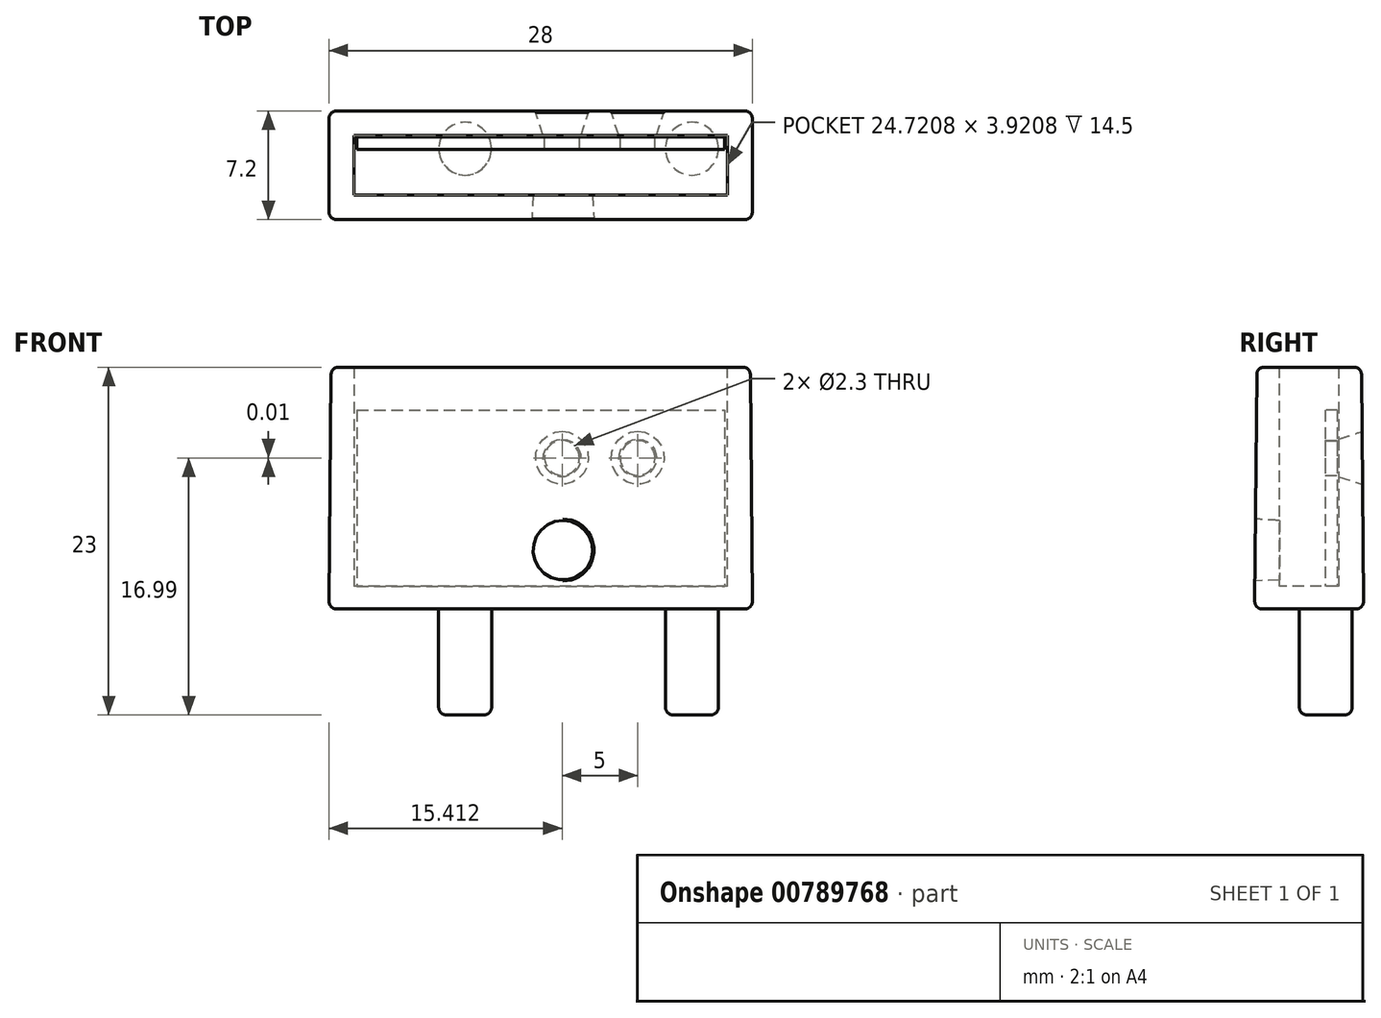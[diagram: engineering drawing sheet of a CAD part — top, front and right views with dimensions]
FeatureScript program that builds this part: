
annotation { "Feature Type Name" : "Feature", "Feature Type Description" : "" }
export const myFeature = defineFeature(function(context is Context, id is Id, definition is map)
    precondition{}
    {
        {
            var Q0;
            Q0=qCreatedBy(makeId("Top.planeOp"),FACE);
            var sketch = newSketch(context, id + "F0", { "sketchPlane" : qUnion([Q0])});
            skLineSegment(sketch, "E0.bottom", {"start": v(-11, 6) * mm, "end": v(17, 6) * mm});
            skLineSegment(sketch, "E0.top", {"start": v(-11, -1.2) * mm, "end": v(17, -1.2) * mm});
            skLineSegment(sketch, "E0.left", {"start": v(-11, 6) * mm, "end": v(-11, -1.2) * mm});
            skLineSegment(sketch, "E0.right", {"start": v(17, 6) * mm, "end": v(17, -1.2) * mm});
            skSolve(sketch);
        }
        {
            var Q0;
            Q0 = qSketchRegion(id + "F0", true);
            extrude(context, id + "F1", {"entities" : qUnion([Q0]), "depth" : 16 * mm, "offsetDistance" : 25 * mm, "hasDraft" : true, "draftAngle" : 0.5 * degree, "draftPullDirection" : true});
        }
        {
            var Q0;
            Q0=makeQuery(id+"F1.opExtrude","CAP_FACE",FACE,{"disambiguationData":[OSD([sQuery(id+"F0.wireOp",EDGE,"E0.bottom"),sQuery(id+"F0.wireOp",EDGE,"E0.top"),sQuery(id+"F0.wireOp",EDGE,"E0.left"),sQuery(id+"F0.wireOp",EDGE,"E0.right")])],"isStart":false});
            var sketch = newSketch(context, id + "F2", { "sketchPlane" : qUnion([Q0])});
            skLineSegment(sketch, "E1.bottom", {"start": v(-9.36, 4.36) * mm, "end": v(15.36, 4.36) * mm});
            skLineSegment(sketch, "E1.top", {"start": v(-9.36, 0.44) * mm, "end": v(15.36, 0.44) * mm});
            skLineSegment(sketch, "E1.left", {"start": v(-9.36, 4.36) * mm, "end": v(-9.36, 0.44) * mm});
            skLineSegment(sketch, "E1.right", {"start": v(15.36, 4.36) * mm, "end": v(15.36, 0.44) * mm});
            skSolve(sketch);
        }
        {
            var Q0;
            Q0=makeQuery(id+"F1.opExtrude","CAP_FACE",FACE,{"disambiguationData":[OSD([sQuery(id+"F0.wireOp",EDGE,"E0.bottom"),sQuery(id+"F0.wireOp",EDGE,"E0.top"),sQuery(id+"F0.wireOp",EDGE,"E0.left"),sQuery(id+"F0.wireOp",EDGE,"E0.right")])],"isStart":true});
            var sketch = newSketch(context, id + "F3", { "sketchPlane" : qUnion([Q0])});
            skCircle(sketch, "E2", {"center": v(13, -3.5) * mm, "radius": 1.75 * mm});
            skCircle(sketch, "E3", {"center": v(-2, -3.5) * mm, "radius": 1.75 * mm});
            skSolve(sketch);
        }
        {
            var Q0;
            Q0 = qSketchRegion(id + "F3", true);
            extrude(context, id + "F4", {"entities" : qUnion([Q0]), "operationType" : NewBodyOperationType.ADD, "depth" : 7 * mm, "offsetDistance" : 25 * mm});
        }
        {
            var Q0;
            Q0=makeQuery(id+"F1.opExtrude","SWEPT_FACE",FACE,{"disambiguationData":[OSD([sQuery(id+"F0.wireOp",EDGE,"E0.bottom")])]});
            var sketch = newSketch(context, id + "F5", { "sketchPlane" : qUnion([Q0])});
            skCircle(sketch, "E4", {"center": v(-6.73, 22.88) * mm, "radius": 1.75 * mm});
            skSolve(sketch);
        }
        {
            var Q0;
            Q0 = qSketchRegion(id + "F5", true);
            extrude(context, id + "F6", {"entities" : qUnion([Q0]), "operationType" : NewBodyOperationType.REMOVE, "oppositeDirection" : true, "depth" : 1.6 * mm, "offsetDistance" : 25 * mm, "hasDraft" : true, "draftAngle" : 18 * degree, "draftPullDirection" : true});
        }
        {
            var Q0;
            Q0=makeQuery(id+"F1.opExtrude","SWEPT_FACE",FACE,{"disambiguationData":[OSD([sQuery(id+"F0.wireOp",EDGE,"E0.bottom")])]});
            var sketch = newSketch(context, id + "F7", { "sketchPlane" : qUnion([Q0])});
            skCircle(sketch, "E5", {"center": v(-9.41, 9.95) * mm, "radius": 1.75 * mm});
            skCircle(sketch, "E6", {"center": v(-4.41, 9.95) * mm, "radius": 1.75 * mm});
            skSolve(sketch);
        }
        {
            var Q0;
            Q0 = qSketchRegion(id + "F7", true);
            extrude(context, id + "F8", {"entities" : qUnion([Q0]), "operationType" : NewBodyOperationType.REMOVE, "oppositeDirection" : true, "depth" : 1.7 * mm, "offsetDistance" : 25 * mm, "hasDraft" : true, "draftAngle" : 18 * degree, "draftPullDirection" : true});
        }
        {
            var Q0;
            Q0 = qSketchRegion(id + "F2", true);
            extrude(context, id + "F9", {"entities" : qUnion([Q0]), "operationType" : NewBodyOperationType.REMOVE, "oppositeDirection" : true, "depth" : 14.5 * mm, "offsetDistance" : 25 * mm, "hasDraft" : true, "draftAngle" : 0 * degree, "draftPullDirection" : true});
        }
        {
            var Q0;
            Q0=makeQuery(id+"F9.boolean.opBoolean","COPY",FACE,{"derivedFrom":makeQuery(id+"F9.opExtrude","CAP_FACE",FACE,{"disambiguationData":[OSD([sQuery(id+"F2.wireOp",EDGE,"E1.bottom"),sQuery(id+"F2.wireOp",EDGE,"E1.top"),sQuery(id+"F2.wireOp",EDGE,"E1.left"),sQuery(id+"F2.wireOp",EDGE,"E1.right")])],"isStart":false})});
            var sketch = newSketch(context, id + "F10", { "sketchPlane" : qUnion([Q0])});
            skLineSegment(sketch, "E7.bottom", {"start": v(-9.16, 4.26) * mm, "end": v(15.16, 4.26) * mm});
            skLineSegment(sketch, "E7.top", {"start": v(-9.16, 3.46) * mm, "end": v(15.16, 3.46) * mm});
            skLineSegment(sketch, "E7.left", {"start": v(-9.16, 4.26) * mm, "end": v(-9.16, 3.46) * mm});
            skLineSegment(sketch, "E7.right", {"start": v(15.16, 4.26) * mm, "end": v(15.16, 3.46) * mm});
            skSolve(sketch);
        }
        {
            var Q0;
            Q0 = qSketchRegion(id + "F10", true);
            extrude(context, id + "F11", {"entities" : qUnion([Q0]), "depth" : 11.66 * mm, "offsetDistance" : 25 * mm});
        }
        {
            var Q0;
            Q0=makeQuery(id+"F11.opExtrude","SWEPT_FACE",FACE,{"disambiguationData":[OSD([sQuery(id+"F10.wireOp",EDGE,"E7.bottom")])]});
            var sketch = newSketch(context, id + "F12", { "sketchPlane" : qUnion([Q0])});
            skCircle(sketch, "E8", {"center": v(-9.41, 9.99) * mm, "radius": 1.15 * mm});
            skCircle(sketch, "E9", {"center": v(-4.41, 10) * mm, "radius": 1.15 * mm});
            skSolve(sketch);
        }
        {
            var Q0;
            Q0 = qSketchRegion(id + "F12", true);
            extrude(context, id + "F13", {"entities" : qUnion([Q0]), "operationType" : NewBodyOperationType.REMOVE, "oppositeDirection" : true, "depth" : 1 * mm, "offsetDistance" : 25 * mm});
        }
        {
            var Q0;
            Q0=makeQuery(id+"F1.opExtrude","CAP_EDGE",EDGE,{"disambiguationData":[OSD([sQuery(id+"F0.wireOp",EDGE,"E0.bottom")])],"isStart":false});
            var Q1;
            Q1=makeQuery(id+"F1.opExtrude","CAP_EDGE",EDGE,{"disambiguationData":[OSD([sQuery(id+"F0.wireOp",EDGE,"E0.left")])],"isStart":false});
            var Q2;
            Q2=makeQuery(id+"F1.opExtrude","SWEPT_EDGE",EDGE,{"disambiguationData":[OSD([sQuery(id+"F0.wireOp",EDGE,"E0.bottom"),sQuery(id+"F0.wireOp",EDGE,"E0.left")])]});
            var Q3;
            Q3=makeQuery(id+"F1.opExtrude","CAP_EDGE",EDGE,{"disambiguationData":[OSD([sQuery(id+"F0.wireOp",EDGE,"E0.bottom")])],"isStart":true});
            var Q4;
            Q4=makeQuery(id+"F1.opExtrude","SWEPT_EDGE",EDGE,{"disambiguationData":[OSD([sQuery(id+"F0.wireOp",EDGE,"E0.bottom"),sQuery(id+"F0.wireOp",EDGE,"E0.right")])]});
            var Q5;
            Q5=makeQuery(id+"F1.opExtrude","SWEPT_EDGE",EDGE,{"disambiguationData":[OSD([sQuery(id+"F0.wireOp",EDGE,"E0.top"),sQuery(id+"F0.wireOp",EDGE,"E0.left")])]});
            var Q6;
            Q6=makeQuery(id+"F1.opExtrude","CAP_EDGE",EDGE,{"disambiguationData":[OSD([sQuery(id+"F0.wireOp",EDGE,"E0.left")])],"isStart":true});
            var Q7;
            Q7=makeQuery(id+"F1.opExtrude","CAP_EDGE",EDGE,{"disambiguationData":[OSD([sQuery(id+"F0.wireOp",EDGE,"E0.top")])],"isStart":true});
            var Q8;
            Q8=makeQuery(id+"F1.opExtrude","CAP_EDGE",EDGE,{"disambiguationData":[OSD([sQuery(id+"F0.wireOp",EDGE,"E0.top")])],"isStart":false});
            var Q9;
            Q9=makeQuery(id+"F1.opExtrude","SWEPT_EDGE",EDGE,{"disambiguationData":[OSD([sQuery(id+"F0.wireOp",EDGE,"E0.top"),sQuery(id+"F0.wireOp",EDGE,"E0.right")])]});
            var Q10;
            Q10=makeQuery(id+"F1.opExtrude","CAP_EDGE",EDGE,{"disambiguationData":[OSD([sQuery(id+"F0.wireOp",EDGE,"E0.right")])],"isStart":false});
            var Q11;
            Q11=makeQuery(id+"F1.opExtrude","CAP_EDGE",EDGE,{"disambiguationData":[OSD([sQuery(id+"F0.wireOp",EDGE,"E0.right")])],"isStart":true});
            var Q12;
            Q12=makeQuery(id+"F4.opExtrude","CAP_EDGE",EDGE,{"disambiguationData":[OSD([sQuery(id+"F3.wireOp",EDGE,"E3")])],"isStart":false});
            var Q13;
            Q13=makeQuery(id+"F4.opExtrude","CAP_EDGE",EDGE,{"disambiguationData":[OSD([sQuery(id+"F3.wireOp",EDGE,"E2")])],"isStart":false});
            fillet(context, id + "F14", {"entities" : qUnion([Q0, Q1, Q2, Q3, Q4, Q5, Q6, Q7, Q8, Q9, Q10, Q11, Q12, Q13]), "radius" : 0.5 * mm, "tangentPropagation" : true, "allowEdgeOverflow" : false});
        }
        {
            var Q0;
            Q0=makeQuery(id+"F1.opExtrude","SWEPT_FACE",FACE,{"disambiguationData":[OSD([sQuery(id+"F0.wireOp",EDGE,"E0.top")])]});
            var sketch = newSketch(context, id + "F15", { "sketchPlane" : qUnion([Q0])});
            skCircle(sketch, "E10", {"center": v(4.47, 3.9) * mm, "radius": 2.05 * mm});
            skSolve(sketch);
        }
        {
            var Q0;
            Q0 = qSketchRegion(id + "F15", true);
            extrude(context, id + "F16", {"entities" : qUnion([Q0]), "operationType" : NewBodyOperationType.REMOVE, "oppositeDirection" : true, "depth" : 1.8 * mm, "offsetDistance" : 25 * mm, "hasDraft" : true, "draftAngle" : 3 * degree, "draftPullDirection" : true});
        }
    });
